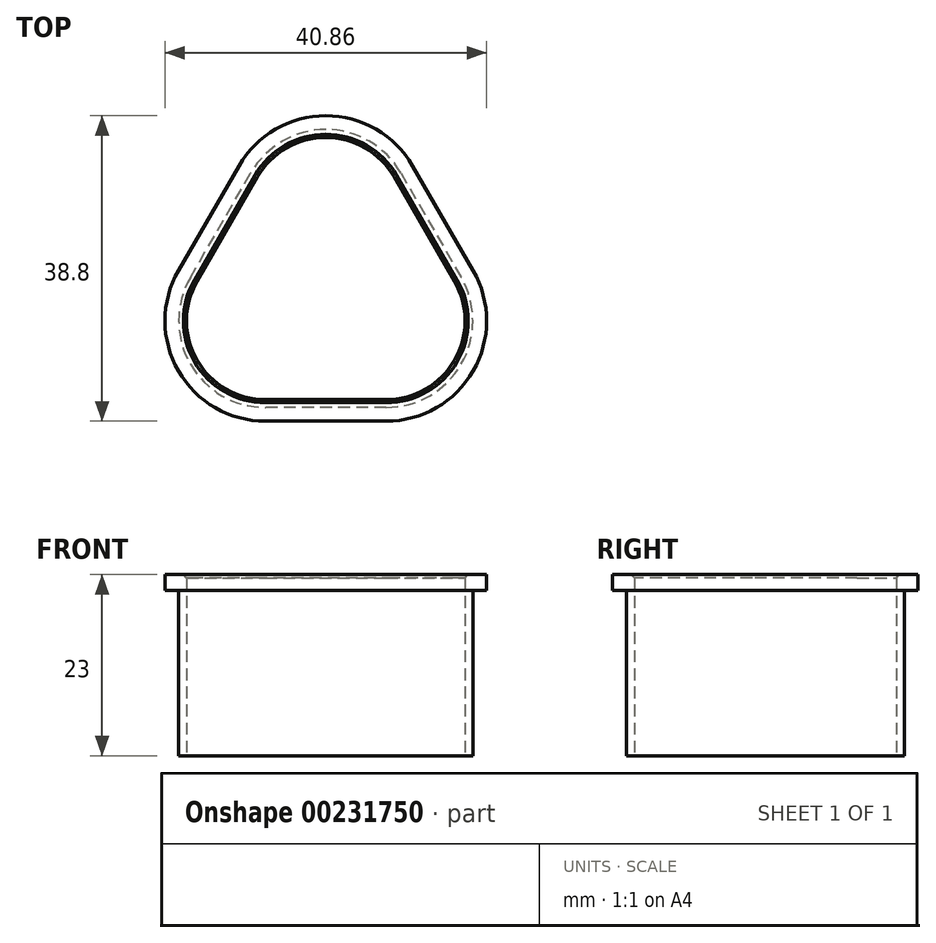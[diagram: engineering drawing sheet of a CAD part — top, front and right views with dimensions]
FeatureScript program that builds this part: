
annotation { "Feature Type Name" : "Feature", "Feature Type Description" : "" }
export const myFeature = defineFeature(function(context is Context, id is Id, definition is map)
    precondition{}
    {
        {
            var Q0;
            Q0=qCreatedBy(makeId("Top.planeOp"),FACE);
            var sketch = newSketch(context, id + "F0", { "sketchPlane" : qUnion([Q0])});
            skLineSegment(sketch, "E0", {"start": v(0, 0) * mm, "end": v(7.68, 0) * mm});
            skLineSegment(sketch, "E1", {"start": v(16.34, 15) * mm, "end": v(8.66, 28.3) * mm});
            skLineSegment(sketch, "E2", {"start": v(-8.66, 28.3) * mm, "end": v(-16.34, 15) * mm});
            skLineSegment(sketch, "E3", {"start": v(-7.68, 0) * mm, "end": v(0, 0) * mm});
            skLineSegment(sketch, "E4", {"start": v(0, 0) * mm, "end": v(0, 43.3) * mm, "construction": true});
            skLineSegment(sketch, "E5", {"start": v(-12.5, 21.65) * mm, "end": v(25, 0) * mm, "construction": true});
            skLineSegment(sketch, "E6", {"start": v(12.5, 21.65) * mm, "end": v(-25, 0) * mm, "construction": true});
            skCircle(sketch, "E7", {"center": v(0, 14.43) * mm, "radius": 12.5 * mm});
            skPoint(sketch, "E8.visualSharp", {"position": v(0, 43.3) * mm});
            skArc(sketch, "E8.filletArc", {"start": v(8.66, 28.3) * mm, "mid": v(0, 33.3) * mm, "end": v(-8.66, 28.3) * mm});
            skPoint(sketch, "E9.visualSharp", {"position": v(-25, 0) * mm});
            skArc(sketch, "E9.filletArc", {"start": v(-16.34, 15) * mm, "mid": v(-16.34, 5) * mm, "end": v(-7.68, 0) * mm});
            skPoint(sketch, "E10.visualSharp", {"position": v(25, 0) * mm});
            skArc(sketch, "E10.filletArc", {"start": v(7.68, 0) * mm, "mid": v(16.34, 5) * mm, "end": v(16.34, 15) * mm});
            skLineSegment(sketch, "E11.0", {"start": v(19.8, 17) * mm, "end": v(12.12, 30.3) * mm});
            skArc(sketch, "E11.1", {"start": v(7.68, -4) * mm, "mid": v(19.8, 3) * mm, "end": v(19.8, 17) * mm});
            skLineSegment(sketch, "E11.2", {"start": v(-12.12, 30.3) * mm, "end": v(-19.8, 17) * mm});
            skArc(sketch, "E11.3", {"start": v(-19.8, 17) * mm, "mid": v(-19.8, 3) * mm, "end": v(-7.68, -4) * mm});
            skLineSegment(sketch, "E11.4", {"start": v(-7.68, -4) * mm, "end": v(0, -4) * mm});
            skArc(sketch, "E11.5", {"start": v(12.12, 30.3) * mm, "mid": v(0, 37.3) * mm, "end": v(-12.12, 30.3) * mm});
            skLineSegment(sketch, "E11.6", {"start": v(0, -4) * mm, "end": v(7.68, -4) * mm});
            skSolve(sketch);
        }
        {
            var Q0;
            Q0=makeQuery(id+"F0.imprint","IMPRINT",FACE,{"disambiguationData":[TD([[makeQuery(id+"F0.imprint","IMPRINT",EDGE,{"derivedFrom":sQuery(id+"F0.wireOp",EDGE,"E0")}),-1.0]])]});
            extrude(context, id + "F1", {"entities" : qUnion([Q0]), "depth" : 25 * mm});
        }
        {
            var Q0;
            Q0=makeQuery(id+"F1.opExtrude","SWEPT_FACE",FACE,{"disambiguationData":[OSD([sQuery(id+"F0.wireOp",EDGE,"E11.2")])]});
            var sketch = newSketch(context, id + "F2", { "sketchPlane" : qUnion([Q0])});
            skCircle(sketch, "E12", {"center": v(-12.5, 12.5) * mm, "radius": 4.3 * mm});
            skPoint(sketch, "E12.centerSnap0", {"position": v(-12.5, 25) * mm});
            skPoint(sketch, "E12.centerSnap1", {"position": v(-20.18, 12.5) * mm});
            skSolve(sketch);
        }
        {
            var Q0;
            Q0=qSketchRegion(id+"F2",true);
            extrude(context, id + "F3", {"entities" : qUnion([Q0]), "operationType" : NewBodyOperationType.REMOVE, "oppositeDirection" : true, "depth" : 3 * mm, "hasSecondDirection" : true, "secondDirectionOppositeDirection" : true, "secondDirectionDepth" : 0.65 * mm});
        }
        {
            var Q0;
            Q0=makeQuery(id+"F1.opExtrude","CAP_FACE",FACE,{"disambiguationData":[OSD([sQuery(id+"F0.wireOp",EDGE,"E0"),sQuery(id+"F0.wireOp",EDGE,"E1"),sQuery(id+"F0.wireOp",EDGE,"E2"),sQuery(id+"F0.wireOp",EDGE,"E3"),sQuery(id+"F0.wireOp",EDGE,"E8.filletArc"),sQuery(id+"F0.wireOp",EDGE,"E9.filletArc"),sQuery(id+"F0.wireOp",EDGE,"E10.filletArc"),sQuery(id+"F0.wireOp",EDGE,"E11.0"),sQuery(id+"F0.wireOp",EDGE,"E11.1"),sQuery(id+"F0.wireOp",EDGE,"E11.2"),sQuery(id+"F0.wireOp",EDGE,"E11.3"),sQuery(id+"F0.wireOp",EDGE,"E11.4"),sQuery(id+"F0.wireOp",EDGE,"E11.5"),sQuery(id+"F0.wireOp",EDGE,"E11.6")])],"isStart":false});
            var sketch = newSketch(context, id + "F4", { "sketchPlane" : qUnion([Q0])});
            skLineSegment(sketch, "E13", {"start": v(-12.5, 21.65) * mm, "end": v(16.34, 5) * mm});
            skLineSegment(sketch, "E14", {"start": v(16.34, 5) * mm, "end": v(0, 0) * mm});
            skLineSegment(sketch, "E15", {"start": v(0, 0) * mm, "end": v(0, 33.3) * mm});
            skCircle(sketch, "E16", {"center": v(0, 14.43) * mm, "radius": 3.2 * mm});
            skSolve(sketch);
        }
        {
            var Q0;
            Q0=makeQuery(id+"F1.opExtrude","CAP_FACE",FACE,{"disambiguationData":[OSD([sQuery(id+"F0.wireOp",EDGE,"E0"),sQuery(id+"F0.wireOp",EDGE,"E1"),sQuery(id+"F0.wireOp",EDGE,"E2"),sQuery(id+"F0.wireOp",EDGE,"E3"),sQuery(id+"F0.wireOp",EDGE,"E8.filletArc"),sQuery(id+"F0.wireOp",EDGE,"E9.filletArc"),sQuery(id+"F0.wireOp",EDGE,"E10.filletArc"),sQuery(id+"F0.wireOp",EDGE,"E11.0"),sQuery(id+"F0.wireOp",EDGE,"E11.1"),sQuery(id+"F0.wireOp",EDGE,"E11.2"),sQuery(id+"F0.wireOp",EDGE,"E11.3"),sQuery(id+"F0.wireOp",EDGE,"E11.4"),sQuery(id+"F0.wireOp",EDGE,"E11.5"),sQuery(id+"F0.wireOp",EDGE,"E11.6")])],"isStart":true});
            var sketch = newSketch(context, id + "F5", { "sketchPlane" : qUnion([Q0])});
            skCircle(sketch, "E17", {"center": v(0, -16.66) * mm, "radius": 40.1 * mm});
            skSolve(sketch);
        }
        {
            var Q0;
            Q0 = qSketchRegion(id + "F5", true);
            extrude(context, id + "F6", {"entities" : qUnion([Q0]), "operationType" : NewBodyOperationType.REMOVE, "oppositeDirection" : true, "depth" : 2 * mm});
        }
        {
            var Q0;
            Q0=makeQuery(id+"F6.boolean.opBoolean","COPY",FACE,{"derivedFrom":makeQuery(id+"F6.opExtrude","CAP_FACE",FACE,{"disambiguationData":[OSD([sQuery(id+"F5.wireOp",EDGE,"E17")])],"isStart":false})});
            var sketch = newSketch(context, id + "F7", { "sketchPlane" : qUnion([Q0])});
            skLineSegment(sketch, "E18.0", {"start": v(-17.2, -15.5) * mm, "end": v(-9.53, -28.8) * mm});
            skLineSegment(sketch, "E18.1", {"start": v(9.53, -28.8) * mm, "end": v(17.2, -15.5) * mm});
            skArc(sketch, "E18.2", {"start": v(17.2, -15.5) * mm, "mid": v(17.2, -4.5) * mm, "end": v(7.68, 1) * mm});
            skArc(sketch, "E18.3", {"start": v(-9.53, -28.8) * mm, "mid": v(0, -34.3) * mm, "end": v(9.53, -28.8) * mm});
            skLineSegment(sketch, "E18.4", {"start": v(7.68, 1) * mm, "end": v(-7.68, 1) * mm});
            skArc(sketch, "E18.5", {"start": v(-7.68, 1) * mm, "mid": v(-17.2, -4.5) * mm, "end": v(-17.2, -15.5) * mm});
            skCircle(sketch, "E19", {"center": v(0, -15.38) * mm, "radius": 28.87 * mm});
            skSolve(sketch);
        }
        {
            var Q0;
            Q0 = qSketchRegion(id + "F7", true);
            extrude(context, id + "F8", {"entities" : qUnion([Q0]), "operationType" : NewBodyOperationType.REMOVE, "oppositeDirection" : true, "depth" : 21 * mm});
        }
        {
            var Q0;
            Q0=makeQuery(id+"F1.opExtrude","CAP_FACE",FACE,{"disambiguationData":[OSD([sQuery(id+"F0.wireOp",EDGE,"E0"),sQuery(id+"F0.wireOp",EDGE,"E1"),sQuery(id+"F0.wireOp",EDGE,"E2"),sQuery(id+"F0.wireOp",EDGE,"E3"),sQuery(id+"F0.wireOp",EDGE,"E8.filletArc"),sQuery(id+"F0.wireOp",EDGE,"E9.filletArc"),sQuery(id+"F0.wireOp",EDGE,"E10.filletArc"),sQuery(id+"F0.wireOp",EDGE,"E11.0"),sQuery(id+"F0.wireOp",EDGE,"E11.1"),sQuery(id+"F0.wireOp",EDGE,"E11.2"),sQuery(id+"F0.wireOp",EDGE,"E11.3"),sQuery(id+"F0.wireOp",EDGE,"E11.4"),sQuery(id+"F0.wireOp",EDGE,"E11.5"),sQuery(id+"F0.wireOp",EDGE,"E11.6")])],"isStart":false});
            var sketch = newSketch(context, id + "F9", { "sketchPlane" : qUnion([Q0])});
            skArc(sketch, "E20.0", {"start": v(-18.72, 16.38) * mm, "mid": v(-18.72, 3.62) * mm, "end": v(-7.68, -2.75) * mm});
            skArc(sketch, "E20.1", {"start": v(7.68, -2.75) * mm, "mid": v(18.72, 3.63) * mm, "end": v(18.72, 16.38) * mm});
            skLineSegment(sketch, "E20.2", {"start": v(18.72, 16.37) * mm, "end": v(11.04, 29.68) * mm});
            skLineSegment(sketch, "E20.3", {"start": v(-7.68, -2.75) * mm, "end": v(7.68, -2.75) * mm});
            skArc(sketch, "E20.4", {"start": v(11.04, 29.68) * mm, "mid": v(0, 36.05) * mm, "end": v(-11.04, 29.68) * mm});
            skLineSegment(sketch, "E20.5", {"start": v(-11.04, 29.68) * mm, "end": v(-18.72, 16.37) * mm});
            skCircle(sketch, "E21", {"center": v(-0.75, 11.02) * mm, "radius": 30.14 * mm});
            skSolve(sketch);
        }
        {
            var Q0;
            Q0 = qSketchRegion(id + "F9", true);
            extrude(context, id + "F10", {"entities" : qUnion([Q0]), "operationType" : NewBodyOperationType.REMOVE, "oppositeDirection" : true, "depth" : 25 * mm});
        }
        {
            var Q0;
            Q0=makeQuery(id+"F10.boolean.opBoolean","COPY",EDGE,{"derivedFrom":makeQuery(id+"F10.opExtrude","CAP_EDGE",EDGE,{"disambiguationData":[OSD([sQuery(id+"F9.wireOp",EDGE,"E20.5")])],"isStart":true})});
            var Q1;
            Q1=makeQuery(id+"F1.opExtrude","CAP_EDGE",EDGE,{"disambiguationData":[OSD([sQuery(id+"F0.wireOp",EDGE,"E2")])],"isStart":false});
            chamfer(context, id + "F11", {"entities" : qUnion([Q0, Q1]), "width" : 0.4 * mm, "tangentPropagation" : true});
        }
    });
